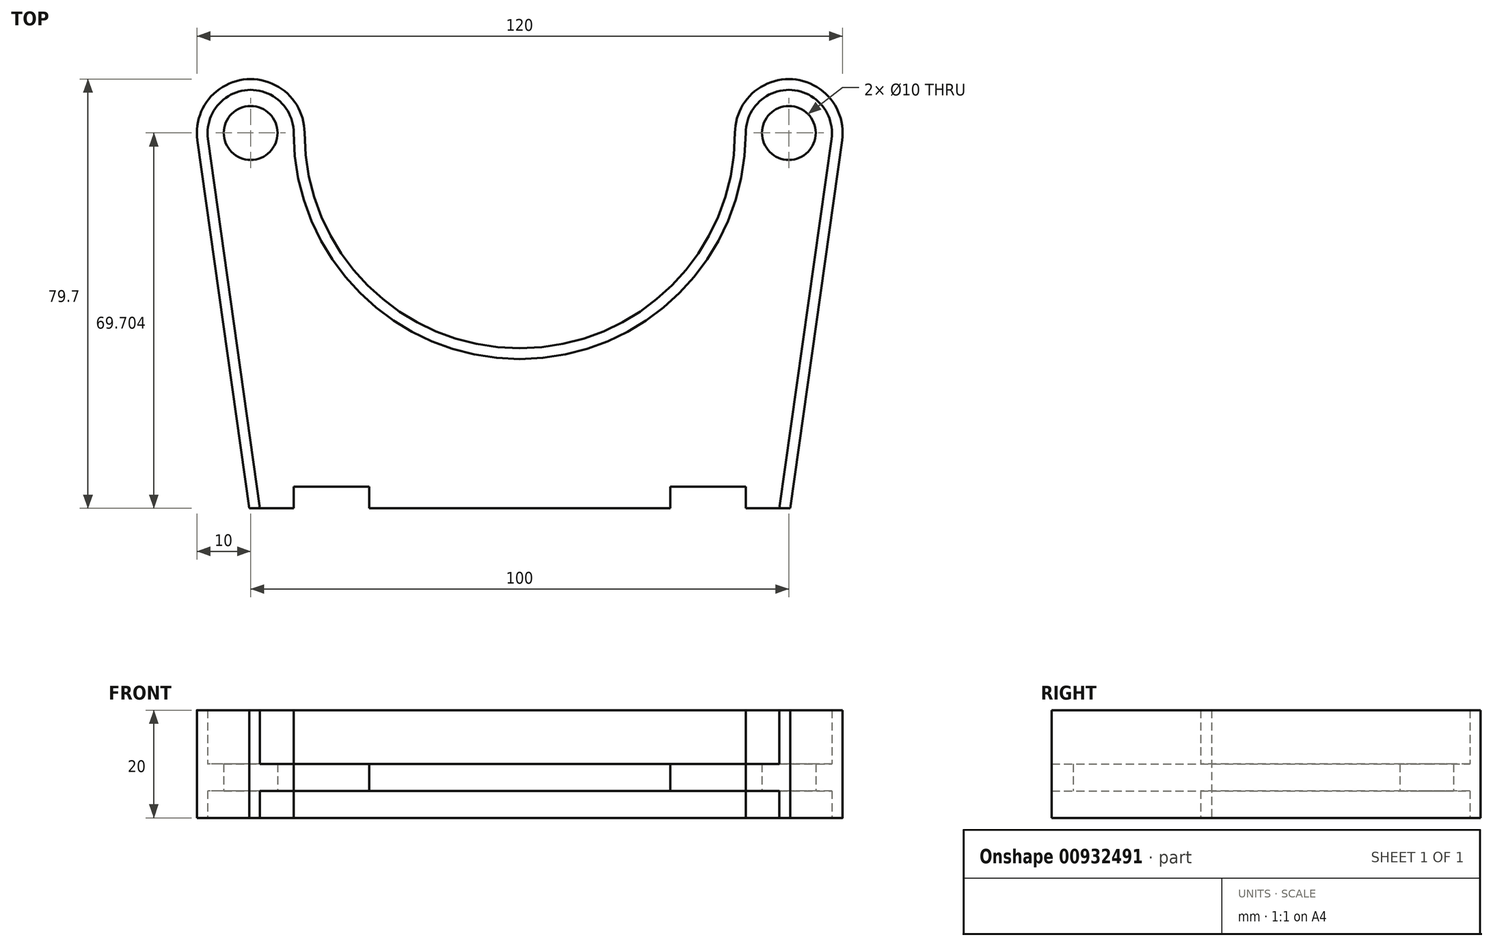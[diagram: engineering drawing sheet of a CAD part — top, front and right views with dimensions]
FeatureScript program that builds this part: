
annotation { "Feature Type Name" : "Feature", "Feature Type Description" : "" }
export const myFeature = defineFeature(function(context is Context, id is Id, definition is map)
    precondition{}
    {
        {
            var Q0;
            Q0=qCreatedBy(makeId("Top.planeOp"),FACE);
            var sketch = newSketch(context, id + "F0", { "sketchPlane" : qUnion([Q0])});
            skLineSegment(sketch, "E0.top", {"start": v(-50, -35.85) * mm, "end": v(-40, -35.85) * mm});
            skPoint(sketch, "E0.middle", {"position": v(0, 0) * mm});
            skCircle(sketch, "E1", {"center": v(-50, 35.85) * mm, "radius": 5 * mm});
            skArc(sketch, "E2.0", {"start": v(-40, 35.85) * mm, "mid": v(-50.7, 45.83) * mm, "end": v(-59.9, 34.46) * mm});
            skArc(sketch, "E3", {"start": v(-40, 35.85) * mm, "mid": v(0, -4.15) * mm, "end": v(40, 35.85) * mm});
            skLineSegment(sketch, "E4.trimOffspring", {"start": v(40, 35.85) * mm, "end": v(42, 35.85) * mm});
            skLineSegment(sketch, "E5", {"start": v(-50.28, -33.85) * mm, "end": v(-59.9, 34.46) * mm});
            skLineSegment(sketch, "E6.top", {"start": v(-40, -31.85) * mm, "end": v(-30, -31.85) * mm});
            skLineSegment(sketch, "E6.left", {"start": v(-40, -35.85) * mm, "end": v(-40, -31.85) * mm});
            skLineSegment(sketch, "E6.right", {"start": v(-30, -35.85) * mm, "end": v(-30, -31.85) * mm});
            skLineSegment(sketch, "E7.trimOffspring", {"start": v(-30, -35.85) * mm, "end": v(30, -35.85) * mm});
            skLineSegment(sketch, "E8.0", {"start": v(-48.26, -33.85) * mm, "end": v(-57.92, 34.74) * mm});
            skLineSegment(sketch, "E8.1", {"start": v(-59.9, -33.85) * mm, "end": v(-50.28, -33.85) * mm});
            skLineSegment(sketch, "E8.2", {"start": v(-42, -33.85) * mm, "end": v(-42, -29.85) * mm});
            skLineSegment(sketch, "E8.3", {"start": v(-42, -29.85) * mm, "end": v(-28, -29.85) * mm});
            skArc(sketch, "E9.0", {"start": v(-42, 35.85) * mm, "mid": v(-50.56, 43.83) * mm, "end": v(-57.92, 34.74) * mm});
            skArc(sketch, "E9.1", {"start": v(-42, 35.85) * mm, "mid": v(0, -6.15) * mm, "end": v(42, 35.85) * mm});
            skLineSegment(sketch, "E10.MirrorCS", {"start": v(-28, -33.85) * mm, "end": v(-28, -29.85) * mm});
            skPoint(sketch, "E11.start.orphan", {"position": v(-35, -31.85) * mm});
            skLineSegment(sketch, "E12.MirrorCS", {"start": v(40, -35.85) * mm, "end": v(40, -31.85) * mm});
            skLineSegment(sketch, "E13.MirrorCS", {"start": v(42, -33.85) * mm, "end": v(42, -29.85) * mm});
            skLineSegment(sketch, "E14.MirrorCS", {"start": v(50, -35.85) * mm, "end": v(40, -35.85) * mm});
            skLineSegment(sketch, "E15.MirrorCS", {"start": v(30, -35.85) * mm, "end": v(30, -31.85) * mm});
            skLineSegment(sketch, "E16.MirrorCS", {"start": v(48.26, -33.85) * mm, "end": v(42, -33.85) * mm});
            skLineSegment(sketch, "E17.MirrorCS", {"start": v(28, -33.85) * mm, "end": v(28, -29.85) * mm});
            skLineSegment(sketch, "E18.MirrorCS", {"start": v(42, -29.85) * mm, "end": v(28, -29.85) * mm});
            skLineSegment(sketch, "E19.MirrorCS", {"start": v(40, -31.85) * mm, "end": v(30, -31.85) * mm});
            skArc(sketch, "E20.MirrorCS", {"start": v(40, 35.85) * mm, "mid": v(0, -4.15) * mm, "end": v(-40, 35.85) * mm});
            skLineSegment(sketch, "E21.MirrorCS", {"start": v(48.26, -33.85) * mm, "end": v(57.92, 34.74) * mm});
            skArc(sketch, "E22.MirrorCS", {"start": v(42, 35.85) * mm, "mid": v(0, -6.15) * mm, "end": v(-42, 35.85) * mm});
            skLineSegment(sketch, "E23.MirrorCS", {"start": v(30, -35.85) * mm, "end": v(-30, -35.85) * mm});
            skArc(sketch, "E24.MirrorCS", {"start": v(40, 35.85) * mm, "mid": v(50.7, 45.83) * mm, "end": v(59.9, 34.46) * mm});
            skPoint(sketch, "E25.MirrorP", {"position": v(35, -31.85) * mm});
            skLineSegment(sketch, "E26.MirrorCS", {"start": v(50.28, -33.85) * mm, "end": v(59.9, 34.46) * mm});
            skCircle(sketch, "E27.MirrorC", {"center": v(50, 35.85) * mm, "radius": 5 * mm});
            skArc(sketch, "E28.MirrorCS", {"start": v(42, 35.85) * mm, "mid": v(50.56, 43.83) * mm, "end": v(57.92, 34.74) * mm});
            skLineSegment(sketch, "E29", {"start": v(-28, -33.85) * mm, "end": v(28, -33.85) * mm});
            skLineSegment(sketch, "E30.trimOffspring", {"start": v(40, -35.85) * mm, "end": v(59.9, -35.85) * mm});
            skLineSegment(sketch, "E31.trimOffspring", {"start": v(-40, -35.85) * mm, "end": v(-59.9, -35.85) * mm});
            skLineSegment(sketch, "E32.bottom", {"start": v(-2.85, 35.85) * mm, "end": v(2.85, 35.85) * mm});
            skLineSegment(sketch, "E32.top", {"start": v(-40, 31.1) * mm, "end": v(-39.72, 31.1) * mm});
            skLineSegment(sketch, "E32.left", {"start": v(-40, 35.85) * mm, "end": v(-40, 31.1) * mm});
            skLineSegment(sketch, "E32.right", {"start": v(39.72, 35.85) * mm, "end": v(39.72, 31.1) * mm});
            skLineSegment(sketch, "E33", {"start": v(-59.9, -33.85) * mm, "end": v(-59.9, -35.85) * mm});
            skPoint(sketch, "E34.orphan", {"position": v(-50, -35.85) * mm});
            skLineSegment(sketch, "E35.trimOffspring", {"start": v(-48.26, -33.85) * mm, "end": v(-42, -33.85) * mm});
            skLineSegment(sketch, "E36", {"start": v(59.9, -33.85) * mm, "end": v(59.9, -35.85) * mm});
            skLineSegment(sketch, "E37.MirrorCS", {"start": v(59.9, -33.85) * mm, "end": v(50.28, -33.85) * mm});
            skPoint(sketch, "E38.orphan", {"position": v(50, -35.85) * mm});
            skLineSegment(sketch, "E39.top", {"start": v(-2.85, -35.85) * mm, "end": v(2.85, -35.85) * mm});
            skLineSegment(sketch, "E39.left", {"start": v(-2.85, 35.85) * mm, "end": v(-2.85, -6.05) * mm});
            skLineSegment(sketch, "E39.right", {"start": v(2.85, 35.85) * mm, "end": v(2.85, -6.05) * mm});
            skSolve(sketch);
        }
        {
            var Q0;
            Q0=makeQuery(id+"F0.imprint","IMPRINT",FACE,{"disambiguationData":[TD([[makeQuery(id+"F0.imprint","IMPRINT",EDGE,{"derivedFrom":sQuery(id+"F0.wireOp",EDGE,"E1")}),-1.0]])]});
            extrude(context, id + "F1", {"entities" : qUnion([Q0]), "endBound" : BoundingType.SYMMETRIC, "depth" : 5 * mm, "offsetDistance" : 25 * mm});
        }
        {
            var Q0;
            Q0=makeQuery(id+"F1.opExtrude","CAP_FACE",FACE,{"disambiguationData":[OSD([sQuery(id+"F0.wireOp",EDGE,"E1"),sQuery(id+"F0.wireOp",EDGE,"E8.0"),sQuery(id+"F0.wireOp",EDGE,"E8.1"),sQuery(id+"F0.wireOp",EDGE,"E8.2"),sQuery(id+"F0.wireOp",EDGE,"E8.3"),sQuery(id+"F0.wireOp",EDGE,"E9.0"),sQuery(id+"F0.wireOp",EDGE,"E10.MirrorCS"),sQuery(id+"F0.wireOp",EDGE,"E13.MirrorCS"),sQuery(id+"F0.wireOp",EDGE,"E16.MirrorCS"),sQuery(id+"F0.wireOp",EDGE,"E17.MirrorCS"),sQuery(id+"F0.wireOp",EDGE,"E18.MirrorCS"),sQuery(id+"F0.wireOp",EDGE,"E21.MirrorCS"),sQuery(id+"F0.wireOp",EDGE,"E22.MirrorCS"),sQuery(id+"F0.wireOp",EDGE,"E27.MirrorC"),sQuery(id+"F0.wireOp",EDGE,"E28.MirrorCS"),sQuery(id+"F0.wireOp",EDGE,"E29")])],"isStart":false});
            var sketch = newSketch(context, id + "F2", { "sketchPlane" : qUnion([Q0])});
            skLineSegment(sketch, "E40.0", {"start": v(50.28, -33.85) * mm, "end": v(59.9, 34.46) * mm});
            skLineSegment(sketch, "E40.1", {"start": v(-50.28, -33.85) * mm, "end": v(-59.9, 34.46) * mm});
            skArc(sketch, "E40.2", {"start": v(-40, 35.85) * mm, "mid": v(-50.7, 45.83) * mm, "end": v(-59.9, 34.46) * mm});
            skArc(sketch, "E40.3", {"start": v(40, 35.85) * mm, "mid": v(0, -4.15) * mm, "end": v(-40, 35.85) * mm});
            skArc(sketch, "E40.4", {"start": v(40, 35.85) * mm, "mid": v(50.7, 45.83) * mm, "end": v(59.9, 34.46) * mm});
            skLineSegment(sketch, "E41", {"start": v(48.26, -33.85) * mm, "end": v(50.28, -33.85) * mm});
            skLineSegment(sketch, "E42", {"start": v(-48.26, -33.85) * mm, "end": v(-50.28, -33.85) * mm});
            skSolve(sketch);
        }
        {
            var Q0;
            Q0=makeQuery(id+"F2.imprint","IMPRINT",FACE,{"disambiguationData":[TD([[makeQuery(id+"F2.imprint","IMPRINT",EDGE,{"derivedFrom":sQuery(id+"F2.wireOp",EDGE,"E40.0")}),1.0]])]});
            var Q1;
            Q1 = qSketchRegion(id + "F4", true);
            extrude(context, id + "F3", {"entities" : qUnion([Q0, Q1]), "operationType" : NewBodyOperationType.ADD, "endBound" : BoundingType.SYMMETRIC, "depth" : 20 * mm, "offsetDistance" : 25 * mm});
        }
    });
